# Revit family: for update_24130XXX_new
name_source: partatom
category: Plumbing Fixtures
revit_build: Autodesk Revit 2018 (Build: 20170223_1515(x64)
units: mm (PartAtom-declared; Revit-internal decimal feet)

## family parameters
Always vertical = No
Cut with Voids When Loaded = No
OmniClass Number = 23.31.17.00
OmniClass Title = Showers
Part Type = Normal
Room Calculation Point = No
Round Connector Dimension = Use Diameter
Shared = No
Work Plane-Based = Yes

## types (4) — shared parameters
Always visible = Yes
BIMobject category = Showers
Connector Description = Water Inlet 12.7mm
Date of publishing = 11/2/2022 12:00:00 AM
Default Elevation = 1219.2 mm  [stored 4 ft]
Description = Pulsify S Overhead shower 105 1jet
Design country = Germany
Diameter = 13 mm
Edition number = 1
IFC Classification = Sanitary Terminal
Manufacturer = Hansgrohe
Manufacturer country = Germany
Manufacturer name = hansgrohe
Masterformat 2014 Code = 22 41 23
Masterformat 2014 Description = Residential Showers
Material 2 = Hansgrohe - Plastic - Graphite
Model = 24130XXX
OmniClass Code = 23-31 17 00
OmniClass Description = Showers
Product Guid = 2f5aeef7-8bb4-454c-a158-f013c7a25cb9
Product SKU = 24130XXX
Product data url = https://bimobject.com
Product family = Pulsify
Product group = Overhead showers
Product name = Pulsify S Overhead shower 105 1jet
Product url = https://www.hansgrohe.com
QR code = https://bimobject.com
UNSPSC Code = 30181503
URL = https://www.hansgrohe.com
Uniclass 2015 Code = Pr_40_20_87_76
Uniclass 2015 Name = Shower heads
Uniformat II Code = D2010
Uniformat II Description = Plumbing Fixtures
Weight Net (Kg) = 442

## per-type parameters (varying)
| type | Material 1 |
| 700 Matte White | Hansgrohe - Metal - 700 Matte White |
| 670 Matte Black | Hansgrohe - Metal - 670 Matte Black |
| 140 Brushed Bronze | Hansgrohe - Metal - 140 Brushed Bronze |
| 000 Chrome | Hansgrohe - Metal - 000 Chrome |

note: [stored X ft] marks values corroborated as IEEE doubles in the binary element streams (Revit-internal decimal feet)

## geometry (parser evidence)
native form markers: Sweep x2
no freeform markers — native parametric forms only
